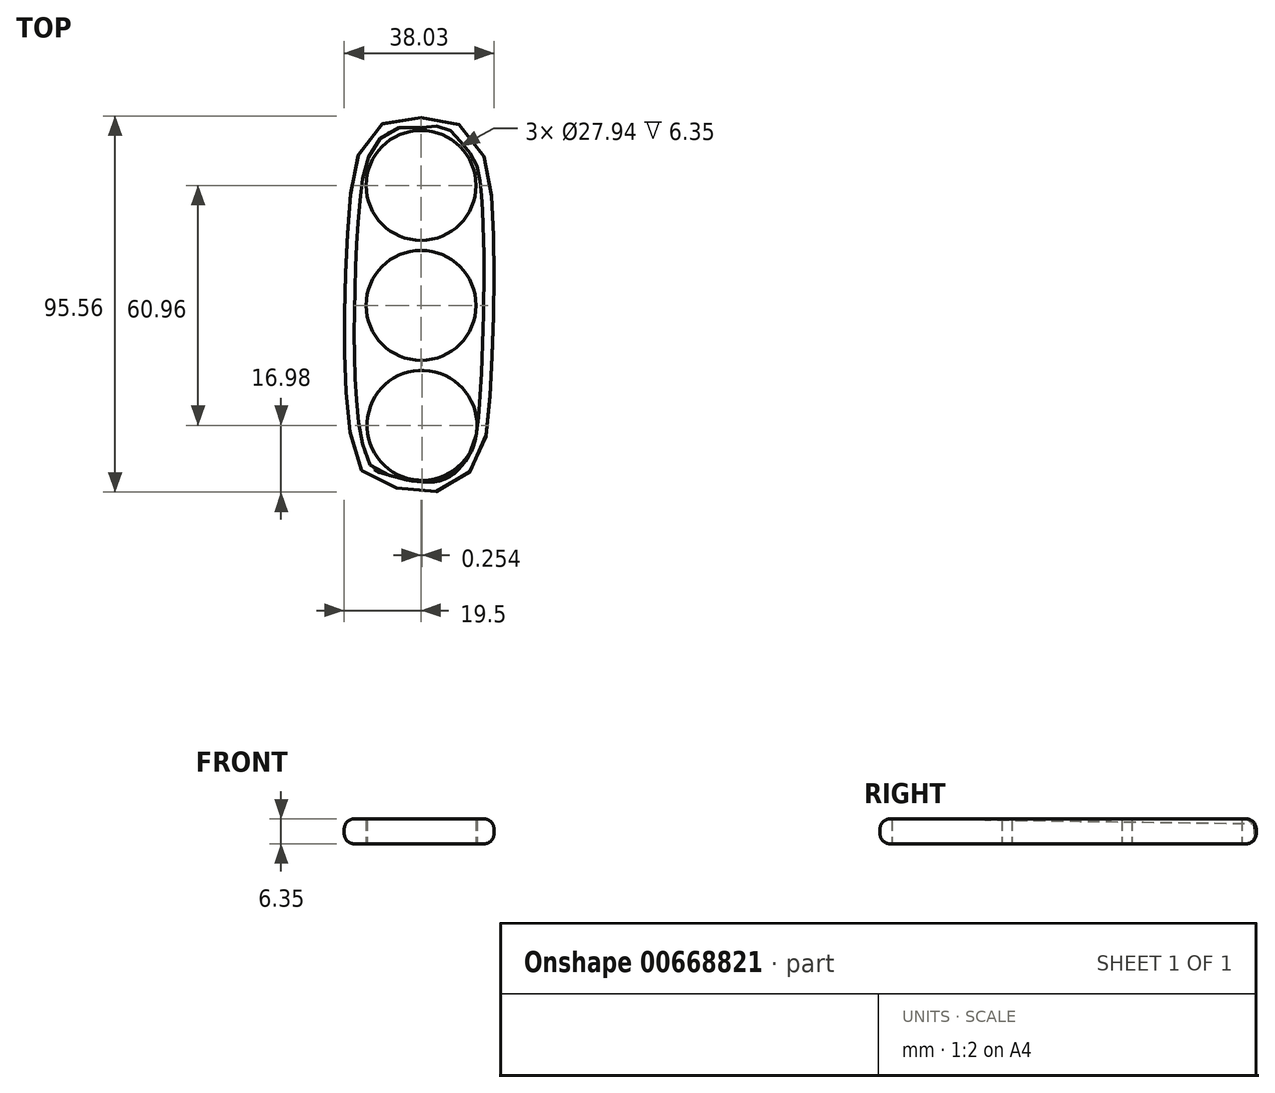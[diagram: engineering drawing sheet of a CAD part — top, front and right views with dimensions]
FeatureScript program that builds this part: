
annotation { "Feature Type Name" : "Feature", "Feature Type Description" : "" }
export const myFeature = defineFeature(function(context is Context, id is Id, definition is map)
    precondition{}
    {
        {
            var Q0;
            Q0=qCreatedBy(makeId("Top.planeOp"),FACE);
            var sketch = newSketch(context, id + "F0", { "sketchPlane" : qUnion([Q0])});
            skCircle(sketch, "E0", {"center": v(0, 0) * mm, "radius": 11.05 * mm});
            skCircle(sketch, "E1", {"center": v(0, 0) * mm, "radius": 13.97 * mm});
            skLineSegment(sketch, "E2", {"start": v(0, 0) * mm, "end": v(0, 30.48) * mm});
            skCircle(sketch, "E3", {"center": v(0, 30.48) * mm, "radius": 11.05 * mm});
            skCircle(sketch, "E4", {"center": v(0, 30.48) * mm, "radius": 13.97 * mm});
            skCircle(sketch, "E5.1.0.0", {"center": v(0.25, -30.48) * mm, "radius": 11.05 * mm});
            skLineSegment(sketch, "E5.direction1", {"start": v(0, 0) * mm, "end": v(0.25, -30.48) * mm, "construction": true});
            skCircle(sketch, "E6.1.0.0", {"center": v(0.25, -30.48) * mm, "radius": 13.97 * mm});
            skPoint(sketch, "E7.0.internal.orphan", {"position": v(0, 47.7) * mm});
            skFitSpline(sketch, "E8", {"points": [v(0, 47.7) * mm, v(-5.84, 47.7) * mm, v(-11.53, 44.85) * mm, v(-14.66, 40.57) * mm, v(-17.23, 33.17) * mm, v(-16.66, -38.58) * mm, v(-9.54, -45.41) * mm, v(0, -47.4) * mm, v(8.68, -45.7) * mm, v(14.38, -39.44) * mm, v(16.94, -30.04) * mm, v(17.23, 33.46) * mm, v(13.24, 41.71) * mm, v(6.98, 47.7) * mm, v(0, 47.7) * mm]});
            skSolve(sketch);
        }
        {
            var Q0;
            Q0 = qSketchRegion(id + "F0", true);
            extrude(context, id + "F1", {"entities" : qUnion([Q0]), "depth" : 6.35 * mm, "offsetDistance" : 25.4 * mm});
        }
        {
            var Q0;
            Q0=makeQuery(id+"F1.opExtrude","CAP_EDGE",EDGE,{"disambiguationData":[OSD([sQuery(id+"F0.wireOp",EDGE,"E8")])],"isStart":false});
            var Q1;
            Q1=makeQuery(id+"F1.opExtrude","CAP_EDGE",EDGE,{"disambiguationData":[OSD([sQuery(id+"F0.wireOp",EDGE,"E8")])],"isStart":true});
            fillet(context, id + "F2", {"entities" : qUnion([Q0, Q1]), "radius" : 2.54 * mm, "tangentPropagation" : true, "allowEdgeOverflow" : false});
        }
    });
